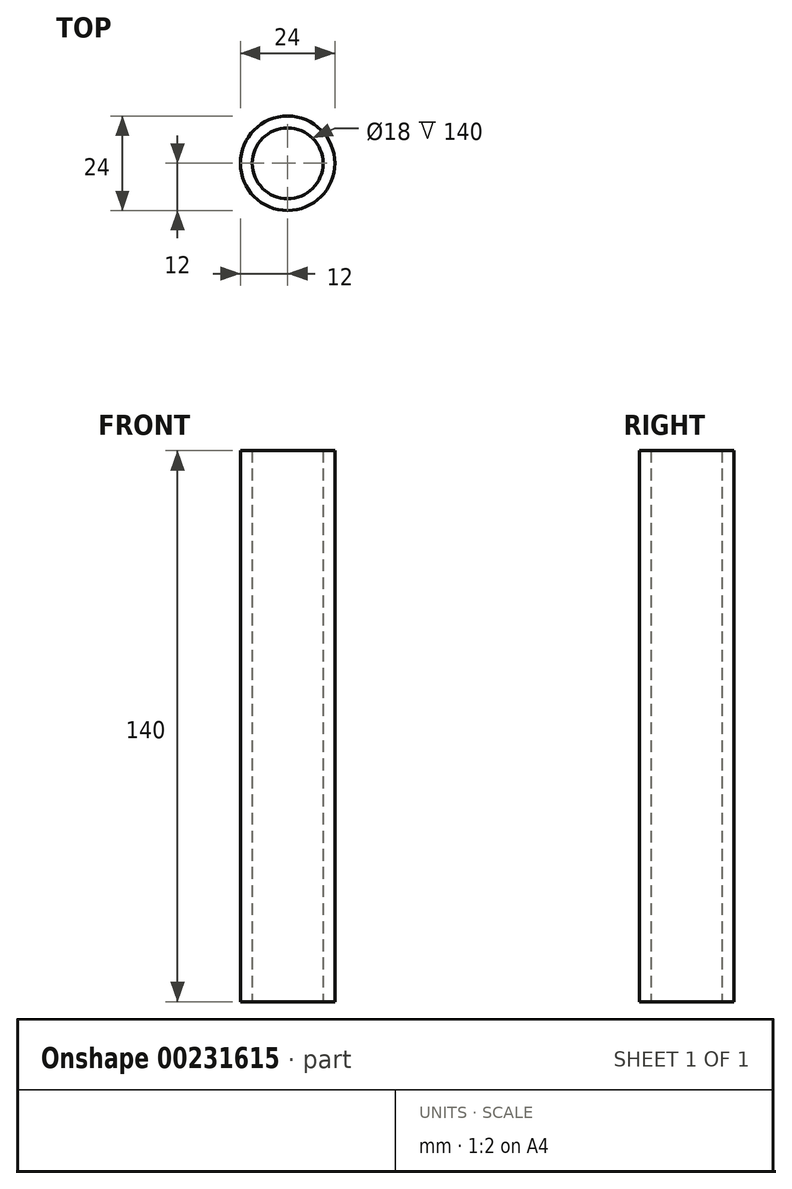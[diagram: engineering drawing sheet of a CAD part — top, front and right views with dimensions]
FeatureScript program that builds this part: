
annotation { "Feature Type Name" : "Feature", "Feature Type Description" : "" }
export const myFeature = defineFeature(function(context is Context, id is Id, definition is map)
    precondition{}
    {
        {
            var Q0;
            Q0=qCreatedBy(makeId("Top.planeOp"),FACE);
            var sketch = newSketch(context, id + "F0", { "sketchPlane" : qUnion([Q0])});
            skCircle(sketch, "E0", {"center": v(0, 0) * mm, "radius": 12 * mm});
            skCircle(sketch, "E1", {"center": v(0, 0) * mm, "radius": 9 * mm});
            skSolve(sketch);
        }
        {
            var Q0;
            Q0=makeQuery(id+"F0.imprint","IMPRINT",FACE,{"disambiguationData":[TD([[makeQuery(id+"F0.imprint","IMPRINT",EDGE,{"derivedFrom":sQuery(id+"F0.wireOp",EDGE,"E0")}),1.0]])]});
            extrude(context, id + "F1", {"entities" : qUnion([Q0]), "depth" : 140 * mm});
        }
    });
